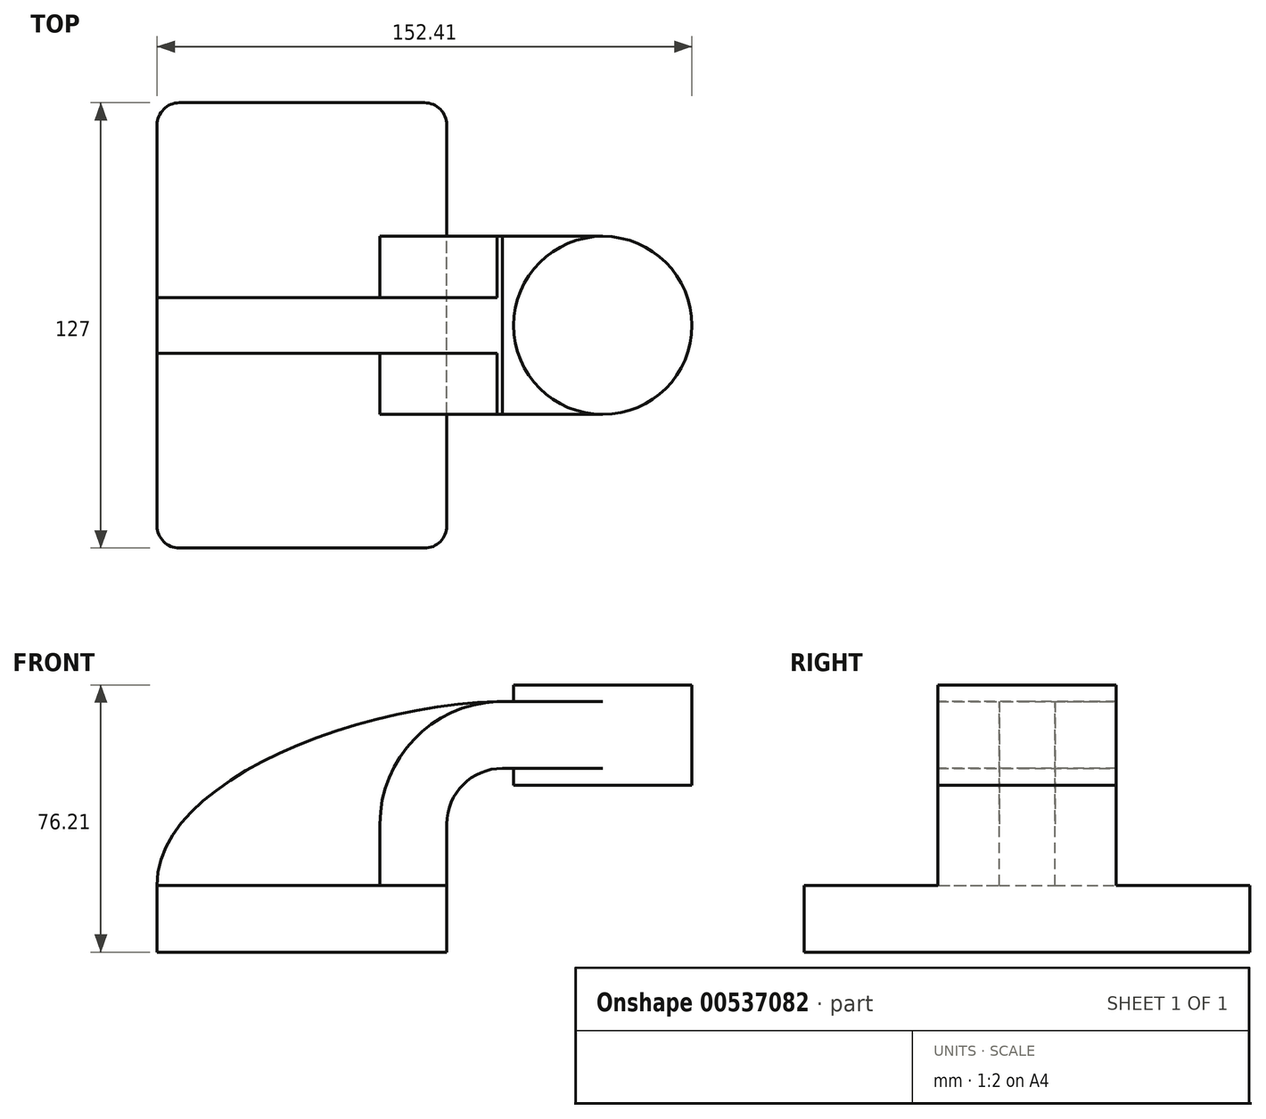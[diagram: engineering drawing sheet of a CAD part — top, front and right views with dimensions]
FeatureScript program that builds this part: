
annotation { "Feature Type Name" : "Feature", "Feature Type Description" : "" }
export const myFeature = defineFeature(function(context is Context, id is Id, definition is map)
    precondition{}
    {
        {
            var Q0;
            Q0=qCreatedBy(makeId("Front.planeOp"),FACE);
            var sketch = newSketch(context, id + "F0", { "sketchPlane" : qUnion([Q0])});
            skLineSegment(sketch, "E0.bottom", {"start": v(41.27, 9.53) * mm, "end": v(-41.28, 9.53) * mm});
            skLineSegment(sketch, "E0.top", {"start": v(41.28, -9.52) * mm, "end": v(-41.27, -9.52) * mm});
            skLineSegment(sketch, "E0.left", {"start": v(41.28, 9.53) * mm, "end": v(41.28, -9.52) * mm});
            skLineSegment(sketch, "E0.right", {"start": v(-41.28, 9.53) * mm, "end": v(-41.27, -9.52) * mm});
            skPoint(sketch, "E0.middle", {"position": v(0, 0) * mm});
            skLineSegment(sketch, "E1.bottom", {"start": v(111.12, 66.68) * mm, "end": v(60.32, 66.68) * mm});
            skLineSegment(sketch, "E1.top", {"start": v(111.12, 38.1) * mm, "end": v(60.33, 38.1) * mm});
            skLineSegment(sketch, "E1.left", {"start": v(111.12, 66.68) * mm, "end": v(111.12, 38.1) * mm});
            skLineSegment(sketch, "E1.right", {"start": v(60.32, 66.68) * mm, "end": v(60.32, 38.1) * mm});
            skPoint(sketch, "E1.middle", {"position": v(85.72, 52.39) * mm});
            skLineSegment(sketch, "E2", {"start": v(41.27, 9.53) * mm, "end": v(41.27, 27) * mm});
            skArc(sketch, "E3", {"start": v(41.27, 27) * mm, "mid": v(45.92, 38.23) * mm, "end": v(57.15, 42.88) * mm});
            skLineSegment(sketch, "E4", {"start": v(57.15, 42.88) * mm, "end": v(85.72, 42.88) * mm});
            skArc(sketch, "E5.0", {"start": v(22.23, 27) * mm, "mid": v(32.45, 51.7) * mm, "end": v(57.15, 61.93) * mm});
            skLineSegment(sketch, "E5.1", {"start": v(22.22, 9.53) * mm, "end": v(22.22, 27) * mm});
            skLineSegment(sketch, "E6", {"start": v(57.15, 61.93) * mm, "end": v(85.72, 61.93) * mm});
            skLineSegment(sketch, "E7", {"start": v(85.72, 38.1) * mm, "end": v(85.72, 66.68) * mm});
            skFitSpline(sketch, "E8", {"points": [v(-41.28, 9.53) * mm, v(57.15, 61.93) * mm], "startDerivative": vector(-1.55, 87.08) * mm, "endDerivative": vector(127.13, 2) * mm});
            skSolve(sketch);
        }
        {
            var Q0;
            Q0=makeQuery(id+"F0.imprint","IMPRINT",FACE,{"disambiguationData":[TD([[makeQuery(id+"F0.imprint","IMPRINT",EDGE,{"derivedFrom":sQuery(id+"F0.wireOp",EDGE,"E0.top")}),-1.0]])]});
            extrude(context, id + "F1", {"entities" : qUnion([Q0]), "endBound" : BoundingType.SYMMETRIC, "depth" : 127 * mm, "offsetDistance" : 25.4 * mm});
        }
        {
            var Q0;
            {var subQ1=sQuery(id+"F0.wireOp",EDGE,"E2");Q0=makeQuery(id+"F0.imprint","IMPRINT",FACE,{"disambiguationData":[TD([[makeQuery(id+"F0.imprint","IMPRINT",EDGE,{"derivedFrom":subQ1}),1.0]])]});}
            var Q1;
            {var subQ0=sQuery(id+"F0.wireOp",EDGE,"E6");var subQ1=sQuery(id+"F0.wireOp",EDGE,"E1.right");var subQ2=makeQuery(id+"F0.imprint","INTERSECT",VERTEX,{"derivedFrom":[subQ1,subQ0]});Q1=makeQuery(id+"F0.imprint","IMPRINT",FACE,{"disambiguationData":[TD([[makeQuery(id+"F0.imprint","IMPRINT",EDGE,{"disambiguationData":[TD([[subQ2,-1.0]])],"derivedFrom":subQ1}),1.0]])]});}
            extrude(context, id + "F2", {"entities" : qUnion([Q0, Q1]), "operationType" : NewBodyOperationType.ADD, "endBound" : BoundingType.SYMMETRIC, "depth" : 50.8 * mm, "offsetDistance" : 25.4 * mm});
        }
        {
            var Q0;
            {var subQ3=sQuery(id+"F0.wireOp",EDGE,"E5.1");Q0=makeQuery(id+"F0.imprint","IMPRINT",FACE,{"disambiguationData":[TD([[makeQuery(id+"F0.imprint","IMPRINT",EDGE,{"derivedFrom":subQ3}),1.0]])]});}
            extrude(context, id + "F3", {"entities" : qUnion([Q0]), "operationType" : NewBodyOperationType.ADD, "endBound" : BoundingType.SYMMETRIC, "depth" : 15.88 * mm, "offsetDistance" : 25.4 * mm});
        }
        {
            var Q0;
            {var subQ0=sQuery(id+"F0.wireOp",EDGE,"E1.left");Q0=makeQuery(id+"F0.imprint","IMPRINT",FACE,{"disambiguationData":[TD([[makeQuery(id+"F0.imprint","IMPRINT",EDGE,{"derivedFrom":subQ0}),-1.0]])]});}
            var Q1;
            Q1=sQuery(id+"F0.wireOp",EDGE,"E7");
            revolve(context, id + "F4", {"operationType" : NewBodyOperationType.ADD, "entities" : qUnion([Q0]), "axis" : qUnion([Q1]), "revolveType" : RevolveType.FULL});
        }
        {
            var Q0;
            Q0=makeQuery(id+"F1.opExtrude","CAP_EDGE",EDGE,{"disambiguationData":[OSD([sQuery(id+"F0.wireOp",EDGE,"E0.left")])],"isStart":false});
            var Q1;
            Q1=makeQuery(id+"F1.opExtrude","CAP_EDGE",EDGE,{"disambiguationData":[OSD([sQuery(id+"F0.wireOp",EDGE,"E0.right")])],"isStart":false});
            var Q2;
            Q2=makeQuery(id+"F1.opExtrude","CAP_EDGE",EDGE,{"disambiguationData":[OSD([sQuery(id+"F0.wireOp",EDGE,"E0.right")])],"isStart":true});
            var Q3;
            Q3=makeQuery(id+"F1.opExtrude","CAP_EDGE",EDGE,{"disambiguationData":[OSD([sQuery(id+"F0.wireOp",EDGE,"E0.left")])],"isStart":true});
            fillet(context, id + "F5", {"entities" : qUnion([Q0, Q1, Q2, Q3]), "radius" : 6.35 * mm, "tangentPropagation" : true, "allowEdgeOverflow" : false});
        }
    });
